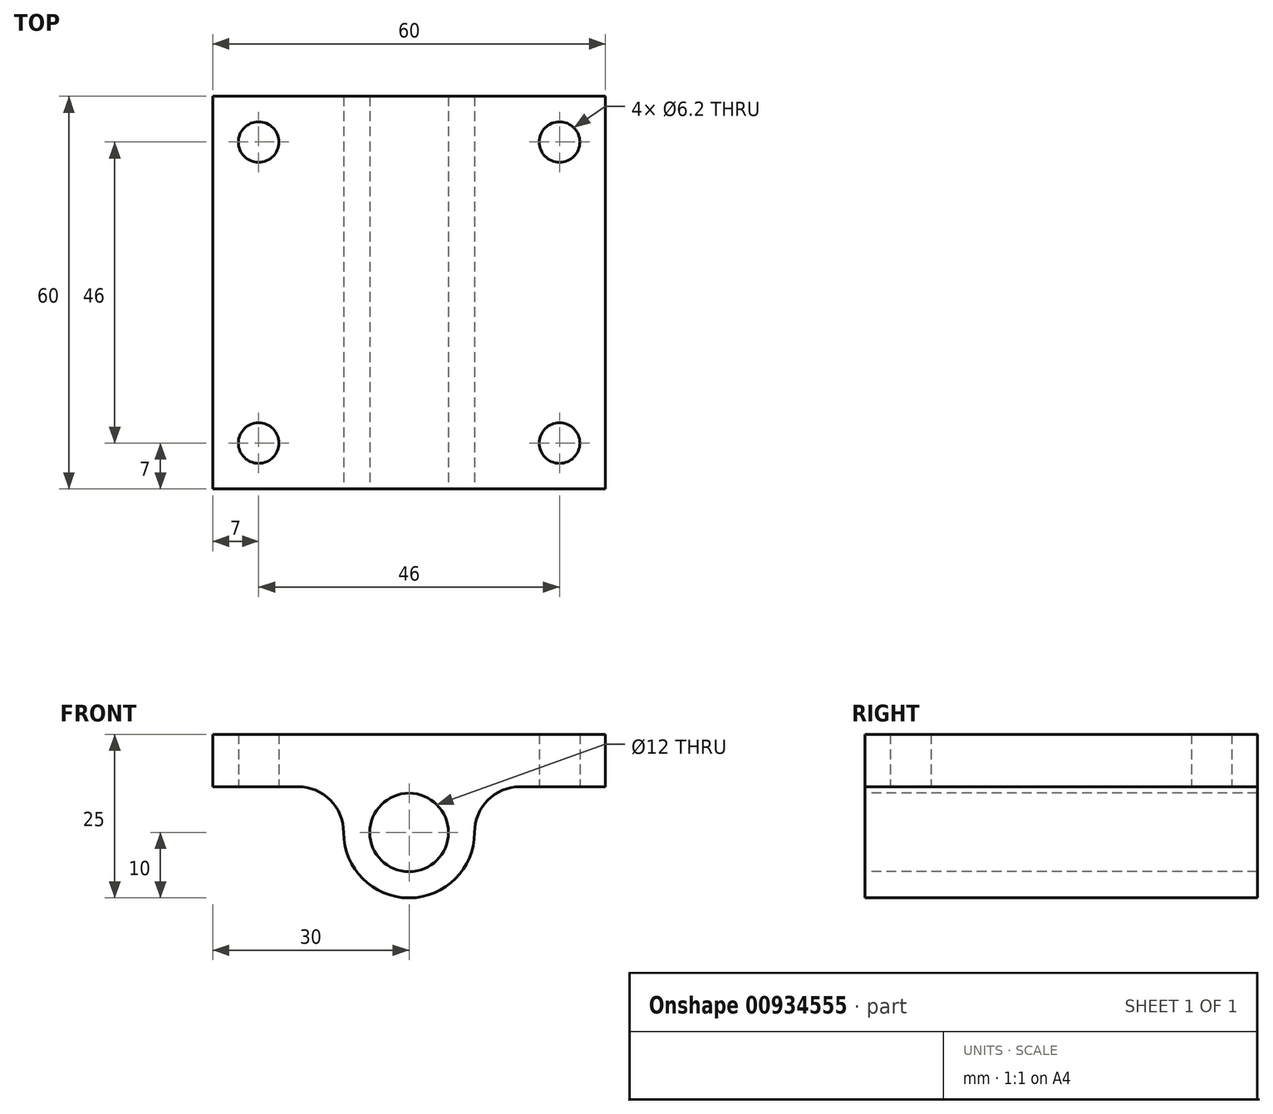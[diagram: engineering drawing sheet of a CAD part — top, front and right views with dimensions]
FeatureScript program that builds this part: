
annotation { "Feature Type Name" : "Feature", "Feature Type Description" : "" }
export const myFeature = defineFeature(function(context is Context, id is Id, definition is map)
    precondition{}
    {
        {
            var Q0;
            Q0=qCreatedBy(makeId("Front.planeOp"),FACE);
            var sketch = newSketch(context, id + "F0", { "sketchPlane" : qUnion([Q0])});
            skArc(sketch, "E0", {"start": v(-7.14, -8) * mm, "mid": v(0, -25) * mm, "end": v(7.14, -8) * mm});
            skLineSegment(sketch, "E1.bottom", {"start": v(-30, 0) * mm, "end": v(30, 0) * mm});
            skLineSegment(sketch, "E1.top", {"start": v(-30, -8) * mm, "end": v(-7.14, -8) * mm});
            skLineSegment(sketch, "E1.left", {"start": v(-30, 0) * mm, "end": v(-30, -8) * mm});
            skLineSegment(sketch, "E1.right", {"start": v(30, 0) * mm, "end": v(30, -8) * mm});
            skLineSegment(sketch, "E2", {"start": v(0, 0) * mm, "end": v(0, -41.66) * mm, "construction": true});
            skLineSegment(sketch, "E3.trimOffspring", {"start": v(7.14, -8) * mm, "end": v(30, -8) * mm});
            skCircle(sketch, "E4", {"center": v(0, -15) * mm, "radius": 6 * mm});
            skSolve(sketch);
        }
        {
            var Q0;
            Q0=makeQuery(id+"F0.imprint","IMPRINT",FACE,{"disambiguationData":[TD([[makeQuery(id+"F0.imprint","IMPRINT",EDGE,{"derivedFrom":sQuery(id+"F0.wireOp",EDGE,"E0")}),1.0]])]});
            extrude(context, id + "F1", {"entities" : qUnion([Q0]), "oppositeDirection" : true, "depth" : 60 * mm, "offsetDistance" : 25 * mm});
        }
        {
            var Q0;
            Q0=makeQuery(id+"F1.opExtrude","SWEPT_EDGE",EDGE,{"disambiguationData":[OSD([sQuery(id+"F0.wireOp",EDGE,"E0"),sQuery(id+"F0.wireOp",EDGE,"E3.trimOffspring")])]});
            var Q1;
            Q1=makeQuery(id+"F1.opExtrude","SWEPT_EDGE",EDGE,{"disambiguationData":[OSD([sQuery(id+"F0.wireOp",EDGE,"E0"),sQuery(id+"F0.wireOp",EDGE,"E1.top")])]});
            fillet(context, id + "F2", {"entities" : qUnion([Q0, Q1]), "radius" : 7 * mm, "tangentPropagation" : true, "allowEdgeOverflow" : false});
        }
        {
            var Q0;
            Q0=makeQuery(id+"F1.opExtrude","SWEPT_FACE",FACE,{"disambiguationData":[OSD([sQuery(id+"F0.wireOp",EDGE,"E1.top")])]});
            var sketch = newSketch(context, id + "F3", { "sketchPlane" : qUnion([Q0])});
            skLineSegment(sketch, "E5.bottom", {"start": v(-30, 0) * mm, "end": v(30, 0) * mm, "construction": true});
            skLineSegment(sketch, "E5.top", {"start": v(-30, -60) * mm, "end": v(30, -60) * mm, "construction": true});
            skLineSegment(sketch, "E5.left", {"start": v(-30, 0) * mm, "end": v(-30, -60) * mm, "construction": true});
            skLineSegment(sketch, "E5.right", {"start": v(30, 0) * mm, "end": v(30, -60) * mm, "construction": true});
            skLineSegment(sketch, "E6.0", {"start": v(-23, -7) * mm, "end": v(-23, -53) * mm, "construction": true});
            skLineSegment(sketch, "E6.1", {"start": v(-23, -7) * mm, "end": v(23, -7) * mm, "construction": true});
            skLineSegment(sketch, "E6.2", {"start": v(23, -7) * mm, "end": v(23, -53) * mm, "construction": true});
            skLineSegment(sketch, "E6.3", {"start": v(-23, -53) * mm, "end": v(23, -53) * mm, "construction": true});
            skCircle(sketch, "E7", {"center": v(-23, -7) * mm, "radius": 3.1 * mm});
            skCircle(sketch, "E8.0.1.0", {"center": v(-23, -53) * mm, "radius": 3.1 * mm});
            skCircle(sketch, "E8.1.0.0", {"center": v(23, -7) * mm, "radius": 3.1 * mm});
            skCircle(sketch, "E8.1.1.0", {"center": v(23, -53) * mm, "radius": 3.1 * mm});
            skSolve(sketch);
        }
        {
            var Q0;
            Q0 = qSketchRegion(id + "F3", true);
            extrude(context, id + "F4", {"entities" : qUnion([Q0]), "operationType" : NewBodyOperationType.REMOVE, "endBound" : BoundingType.THROUGH_ALL, "oppositeDirection" : true, "depth" : 25 * mm, "offsetDistance" : 25 * mm});
        }
    });
